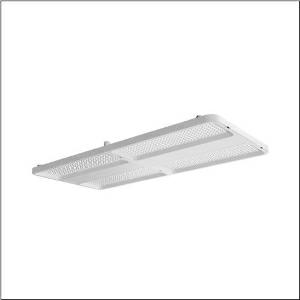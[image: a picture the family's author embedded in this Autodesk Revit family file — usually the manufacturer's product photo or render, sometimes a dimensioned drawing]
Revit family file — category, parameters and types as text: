
# Revit family: highbay_21_maxi_52hn12db6lda
name_source: partatom
category: Lighting Fixtures
units: mm (PartAtom-declared; Revit-internal decimal feet)

## family parameters
Cut with Voids When Loaded = No
Host = Face
Light Source = No
Part Type = Normal
Room Calculation Point = No
Round Connector Dimension = Use Diameter
Shared = No

## types (1)
- --- (1 x LED, 4100 lm, 22.6 W, 6500K)
    Apparent Load = 23 VA
    CIE Flux Codes = 90 98 100 100 100
    Color Rendering = 80
    Color Temperature = 6500K
    Default Elevation = 1800 mm
    Description = high bay luminaire Highbay 21 maxi; direct symmetric wide distribution, light control with lens of PMMA; UGR ≤ 22 (X = 4H | Y = 8H | S = 0.25H | reflection values 70/50/20); luminous flux: 27.140lm; light colour: 865, colour temperature: 6500K, MacAdam ≤ 3 SDCM (initial), colour rendering: CRI > 80; luminous efficacy: 188,5lm/W; rated service life: 75.000h (L80/B50) at AT= ta max; control: DALI 2; luminaire connection: terminal, 5-pole, max. 2.5mm² (cable entry for one cable, Ø 8.5..16mm); mains connection: 230..240V, AC/DC 0/50..60Hz; connected load: 144W; protection rating (complete): IP66; insulation class (complete): insulation class I (protective earthing); protection symbol: D; impact resistance: IK08; certification: CE, ENEC, VDE, UKCA; luminaire for central battery installations according to DIN EN 60598-2-22, internal wiring halogen-free; luminaire corresponds to IFS (International Featured Standards) requirements for safety and quality in the food industry; LABS conformity tested according to VDMA 24364:2018-05; housing frame of high-performance plastic PA6, matt traffic white (RAL 9016); cover of PMMA; dimension (LxWxH): 946 x 442 x 72mm; permissible operating ambient temperature: -40..+65°C (reducing of maximum allowable ambient temperature of 5°C with ceiling mounting); packaging unit: 1 piece; (delivery without accessories; please order mounting accessories separately)
    Height = 72 mm  [stored 0.23622 ft]
    Lamp = 1 x LED
    Lamp Light Flux = 4100 lm
    Lamp Power = 22.6 W
    Lamp count = 1
    Length = 946 mm
    Luminous efficacy = 181 lm/W
    Manufacturer = Siteco
    ModVariant = No
    Model = 52HN12DB6LDA
    Mounting Place = Ceiling
    Mounting Type = Pendant
    Number of Poles = 1
    OnlyDefault = Yes
    Power Factor = 1
    Product Name = Highbay 21 maxi
    Product group = high bay luminaire
    ProductGroupID = 901
    Protection Class = Protection class I
    Protection Degree = IP 66
    RLX_Detail_Level = 1
    RLX_Emergency_Light_Flux = 0 lm
    RLX_Emergency_Type = 0
    RLX_Emergency_Type_DB = No
    RlxData = <blob elided: 127933 chars, md5=1617ef68>
    Socket = socket
    Standby Power = 0 W
    System Light Flux = 4100 lm
    System Power = 23 W
    Type Comments = : DC mode (central or group accumulator) initial emergency light level
    Type Image = l_1363244.jpg
    URL = http://relux.com
    VarID = @adj_002583
    Voltage = 0 V
    Weight = 0.00 kg
    Width = 442 mm

note: [stored X ft] marks values corroborated as IEEE doubles in the binary element streams (Revit-internal decimal feet)

## geometry (parser evidence)
native form markers: Blend x4, Sweep x10
no freeform markers — native parametric forms only
